SOLIDWORKS PART (.sldprt)
format: sldprt  version: not decoded by parser v0  size: 425,984 bytes
history: native  units: mm
features: plane x3, sketch x3, cut_extrude x2, material x1, revolve x1, shell x1 (+10 scaffold rows collapsed)
feature tree (21):
  scaffold x10  (default folders/planes/origin — collapsed)
  material  "材质 <未指定>"
  plane  "前视基准面"
  plane  "上视基准面"
  plane  "右视基准面"
  sketch  "草图1"  dims[D1=75.0mm]
  revolve  "旋转1"  Angle=360deg
  shell  "抽壳1"  Thickness=0.5mm
  sketch  "草图2"  dims[c1.D21=~144.605097mm c1.D22=74.0mm c1.D23=70.0mm c2.D21=~72.302549mm c2.D24=~30.267326mm c2.D1=0.0mm c2.D2=0.0mm c2.D3=0.0mm c2.D4=0.0mm c2.D5=0.0mm c2.D6=0.0mm c2.D7=0.0mm c2.D8=0.0mm c2.D9=0.0mm c2.D10=0.0mm c2.D11=0.0mm c2.D12=0.0mm c2.D13=0.0mm c2.D14=0.0mm c2.D15=0.0mm c2.D16=0.0mm c2.D17=0.0mm c2.D18=0.0mm c2.D19=0.0mm c2.D20=0.0mm c3.D21=14.0]
  cut_extrude  "切除-拉伸1"  Depth=255mm
  sketch  "草图4"  dims[D1=22.0mm D2=30.0mm D3=~43.135602mm]
  cut_extrude  "切除-拉伸2"  Depth=20mm
decode coverage: 7 of 7 modeling features carry decoded parameters
note: ~ marks probable driven/reference dimensions
note: suppression state not decoded; provenance and decode notes live in map.json
